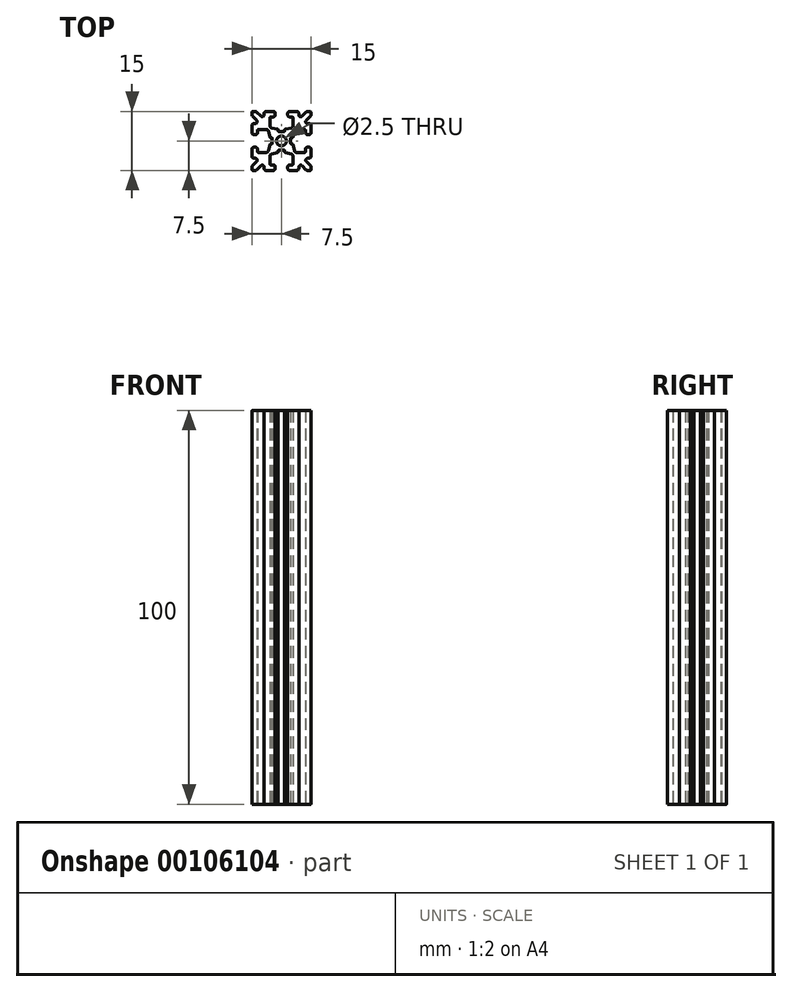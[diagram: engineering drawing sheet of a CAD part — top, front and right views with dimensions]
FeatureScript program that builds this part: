
annotation { "Feature Type Name" : "Feature", "Feature Type Description" : "" }
export const myFeature = defineFeature(function(context is Context, id is Id, definition is map)
    precondition{}
    {
        {
            var Q0;
            Q0=qCreatedBy(makeId("Top.planeOp"),FACE);
            var sketch = newSketch(context, id + "F0", { "sketchPlane" : qUnion([Q0])});
            skCircle(sketch, "E0", {"center": v(0, 0) * mm, "radius": 1.25 * mm});
            skLineSegment(sketch, "E1", {"start": v(0.63, -2.35) * mm, "end": v(-0.63, -2.35) * mm});
            skLineSegment(sketch, "E2", {"start": v(-0.83, -2.55) * mm, "end": v(-0.83, -2.77) * mm});
            skLineSegment(sketch, "E3", {"start": v(-0.98, -2.97) * mm, "end": v(-2.5, -3.31) * mm});
            skLineSegment(sketch, "E4", {"start": v(-2.9, -3.8) * mm, "end": v(-2.9, -5.9) * mm});
            skLineSegment(sketch, "E5", {"start": v(-2.7, -6.1) * mm, "end": v(-2.1, -6.1) * mm});
            skLineSegment(sketch, "E6", {"start": v(-1.6, -6.6) * mm, "end": v(-1.6, -7) * mm});
            skLineSegment(sketch, "E7", {"start": v(-4.4, -7) * mm, "end": v(-4.4, -6.67) * mm});
            skLineSegment(sketch, "E8", {"start": v(-5.25, -6.31) * mm, "end": v(-6.3, -7.35) * mm});
            skLineSegment(sketch, "E9", {"start": v(-7.35, -6.3) * mm, "end": v(-6.31, -5.25) * mm});
            skLineSegment(sketch, "E10", {"start": v(-6.67, -4.4) * mm, "end": v(-7, -4.4) * mm});
            skLineSegment(sketch, "E11", {"start": v(-7.5, -2.1) * mm, "end": v(-7.5, -3.9) * mm});
            skLineSegment(sketch, "E12", {"start": v(-7, -1.6) * mm, "end": v(-6.6, -1.6) * mm});
            skLineSegment(sketch, "E13", {"start": v(-6.1, -2.1) * mm, "end": v(-6.1, -2.7) * mm});
            skLineSegment(sketch, "E14", {"start": v(-5.9, -2.9) * mm, "end": v(-3.8, -2.9) * mm});
            skLineSegment(sketch, "E15", {"start": v(-3.31, -2.5) * mm, "end": v(-2.97, -0.98) * mm});
            skLineSegment(sketch, "E16", {"start": v(-2.77, -0.83) * mm, "end": v(-2.55, -0.83) * mm});
            skLineSegment(sketch, "E17", {"start": v(-2.35, -0.63) * mm, "end": v(-2.35, 0.63) * mm});
            skLineSegment(sketch, "E18", {"start": v(-2.55, 0.83) * mm, "end": v(-2.77, 0.83) * mm});
            skLineSegment(sketch, "E19", {"start": v(-2.97, 0.98) * mm, "end": v(-3.31, 2.5) * mm});
            skLineSegment(sketch, "E20", {"start": v(-3.8, 2.9) * mm, "end": v(-5.9, 2.9) * mm});
            skLineSegment(sketch, "E21", {"start": v(-6.1, 2.7) * mm, "end": v(-6.1, 2.1) * mm});
            skLineSegment(sketch, "E22", {"start": v(-6.6, 1.6) * mm, "end": v(-7, 1.6) * mm});
            skLineSegment(sketch, "E23", {"start": v(-7, 4.4) * mm, "end": v(-6.67, 4.4) * mm});
            skLineSegment(sketch, "E24", {"start": v(-6.31, 5.25) * mm, "end": v(-7.35, 6.3) * mm});
            skLineSegment(sketch, "E25", {"start": v(-6.3, 7.35) * mm, "end": v(-5.25, 6.31) * mm});
            skLineSegment(sketch, "E26", {"start": v(-4.4, 6.67) * mm, "end": v(-4.4, 7) * mm});
            skLineSegment(sketch, "E27", {"start": v(-1.6, 7) * mm, "end": v(-1.6, 6.6) * mm});
            skLineSegment(sketch, "E28", {"start": v(-2.1, 6.1) * mm, "end": v(-2.7, 6.1) * mm});
            skLineSegment(sketch, "E29", {"start": v(-2.9, 5.9) * mm, "end": v(-2.9, 3.8) * mm});
            skLineSegment(sketch, "E30", {"start": v(-2.5, 3.31) * mm, "end": v(-0.98, 2.97) * mm});
            skLineSegment(sketch, "E31", {"start": v(-0.83, 2.77) * mm, "end": v(-0.83, 2.55) * mm});
            skLineSegment(sketch, "E32", {"start": v(-0.63, 2.35) * mm, "end": v(0.63, 2.35) * mm});
            skLineSegment(sketch, "E33", {"start": v(0.83, 2.55) * mm, "end": v(0.83, 2.77) * mm});
            skLineSegment(sketch, "E34", {"start": v(0.98, 2.97) * mm, "end": v(2.5, 3.31) * mm});
            skLineSegment(sketch, "E35", {"start": v(2.9, 3.8) * mm, "end": v(2.9, 5.9) * mm});
            skLineSegment(sketch, "E36", {"start": v(2.7, 6.1) * mm, "end": v(2.1, 6.1) * mm});
            skLineSegment(sketch, "E37", {"start": v(1.6, 6.6) * mm, "end": v(1.6, 7) * mm});
            skLineSegment(sketch, "E38", {"start": v(4.4, 7) * mm, "end": v(4.4, 6.67) * mm});
            skLineSegment(sketch, "E39", {"start": v(5.25, 6.31) * mm, "end": v(6.3, 7.35) * mm});
            skLineSegment(sketch, "E40", {"start": v(7.25, 7.5) * mm, "end": v(6.65, 7.5) * mm});
            skLineSegment(sketch, "E41", {"start": v(7.35, 6.3) * mm, "end": v(6.31, 5.25) * mm});
            skLineSegment(sketch, "E42", {"start": v(6.67, 4.4) * mm, "end": v(7, 4.4) * mm});
            skLineSegment(sketch, "E43", {"start": v(7, 1.6) * mm, "end": v(6.6, 1.6) * mm});
            skLineSegment(sketch, "E44", {"start": v(6.1, 2.1) * mm, "end": v(6.1, 2.7) * mm});
            skLineSegment(sketch, "E45", {"start": v(5.9, 2.9) * mm, "end": v(3.8, 2.9) * mm});
            skLineSegment(sketch, "E46", {"start": v(3.31, 2.5) * mm, "end": v(2.97, 0.98) * mm});
            skLineSegment(sketch, "E47", {"start": v(2.77, 0.83) * mm, "end": v(2.55, 0.83) * mm});
            skLineSegment(sketch, "E48", {"start": v(2.35, 0.63) * mm, "end": v(2.35, -0.63) * mm});
            skLineSegment(sketch, "E49", {"start": v(2.55, -0.83) * mm, "end": v(2.77, -0.83) * mm});
            skLineSegment(sketch, "E50", {"start": v(2.97, -0.98) * mm, "end": v(3.31, -2.5) * mm});
            skLineSegment(sketch, "E51", {"start": v(3.8, -2.9) * mm, "end": v(5.9, -2.9) * mm});
            skLineSegment(sketch, "E52", {"start": v(6.1, -2.7) * mm, "end": v(6.1, -2.1) * mm});
            skLineSegment(sketch, "E53", {"start": v(6.6, -1.6) * mm, "end": v(7, -1.6) * mm});
            skLineSegment(sketch, "E54", {"start": v(7.5, -3.9) * mm, "end": v(7.5, -2.1) * mm});
            skLineSegment(sketch, "E55", {"start": v(7, -4.4) * mm, "end": v(6.67, -4.4) * mm});
            skLineSegment(sketch, "E56", {"start": v(6.31, -5.25) * mm, "end": v(7.35, -6.3) * mm});
            skLineSegment(sketch, "E57", {"start": v(6.65, -7.5) * mm, "end": v(7.25, -7.5) * mm});
            skLineSegment(sketch, "E58", {"start": v(6.3, -7.35) * mm, "end": v(5.25, -6.31) * mm});
            skLineSegment(sketch, "E59", {"start": v(4.4, -6.67) * mm, "end": v(4.4, -7) * mm});
            skLineSegment(sketch, "E60", {"start": v(1.6, -7) * mm, "end": v(1.6, -6.6) * mm});
            skLineSegment(sketch, "E61", {"start": v(2.1, -6.1) * mm, "end": v(2.7, -6.1) * mm});
            skLineSegment(sketch, "E62", {"start": v(2.9, -5.9) * mm, "end": v(2.9, -3.8) * mm});
            skLineSegment(sketch, "E63", {"start": v(2.5, -3.31) * mm, "end": v(0.98, -2.97) * mm});
            skLineSegment(sketch, "E64", {"start": v(0.83, -2.77) * mm, "end": v(0.83, -2.55) * mm});
            skLineSegment(sketch, "E65", {"start": v(-7.5, 3.9) * mm, "end": v(-7.5, 2.1) * mm});
            skLineSegment(sketch, "E66", {"start": v(-6.65, 7.5) * mm, "end": v(-7.25, 7.5) * mm});
            skLineSegment(sketch, "E67", {"start": v(-3.9, -7.5) * mm, "end": v(-2.1, -7.5) * mm});
            skLineSegment(sketch, "E68", {"start": v(7.5, 2.1) * mm, "end": v(7.5, 3.9) * mm});
            skLineSegment(sketch, "E69", {"start": v(-7.5, 7.25) * mm, "end": v(-7.5, 6.65) * mm});
            skLineSegment(sketch, "E70", {"start": v(7.5, -7.25) * mm, "end": v(7.5, -6.65) * mm});
            skLineSegment(sketch, "E71", {"start": v(7.5, 6.65) * mm, "end": v(7.5, 7.25) * mm});
            skLineSegment(sketch, "E72", {"start": v(-2.1, 7.5) * mm, "end": v(-3.9, 7.5) * mm});
            skLineSegment(sketch, "E73", {"start": v(-7.5, -6.65) * mm, "end": v(-7.5, -7.25) * mm});
            skLineSegment(sketch, "E74", {"start": v(3.9, 7.5) * mm, "end": v(2.1, 7.5) * mm});
            skLineSegment(sketch, "E75", {"start": v(2.1, -7.5) * mm, "end": v(3.9, -7.5) * mm});
            skLineSegment(sketch, "E76", {"start": v(-7.25, -7.5) * mm, "end": v(-6.65, -7.5) * mm});
            skArc(sketch, "E77", {"start": v(0.83, -2.55) * mm, "mid": v(0.77, -2.4) * mm, "end": v(0.63, -2.35) * mm});
            skArc(sketch, "E78", {"start": v(-0.63, -2.35) * mm, "mid": v(-0.77, -2.4) * mm, "end": v(-0.83, -2.55) * mm});
            skArc(sketch, "E79", {"start": v(-0.98, -2.97) * mm, "mid": v(-0.87, -2.9) * mm, "end": v(-0.83, -2.77) * mm});
            skArc(sketch, "E80", {"start": v(-2.5, -3.31) * mm, "mid": v(-2.8, -3.49) * mm, "end": v(-2.9, -3.8) * mm});
            skArc(sketch, "E81", {"start": v(-2.9, -5.9) * mm, "mid": v(-2.84, -6.04) * mm, "end": v(-2.7, -6.1) * mm});
            skArc(sketch, "E82", {"start": v(-1.6, -6.6) * mm, "mid": v(-1.75, -6.25) * mm, "end": v(-2.1, -6.1) * mm});
            skArc(sketch, "E83", {"start": v(-2.1, -7.5) * mm, "mid": v(-1.75, -7.35) * mm, "end": v(-1.6, -7) * mm});
            skArc(sketch, "E84", {"start": v(-4.4, -7) * mm, "mid": v(-4.25, -7.35) * mm, "end": v(-3.9, -7.5) * mm});
            skArc(sketch, "E85", {"start": v(-4.4, -6.67) * mm, "mid": v(-4.7, -6.2) * mm, "end": v(-5.25, -6.31) * mm});
            skArc(sketch, "E86", {"start": v(-6.65, -7.5) * mm, "mid": v(-6.46, -7.46) * mm, "end": v(-6.3, -7.35) * mm});
            skArc(sketch, "E87", {"start": v(-7.5, -7.25) * mm, "mid": v(-7.43, -7.43) * mm, "end": v(-7.25, -7.5) * mm});
            skArc(sketch, "E88", {"start": v(-7.35, -6.3) * mm, "mid": v(-7.46, -6.46) * mm, "end": v(-7.5, -6.65) * mm});
            skArc(sketch, "E89", {"start": v(-6.31, -5.25) * mm, "mid": v(-6.2, -4.7) * mm, "end": v(-6.67, -4.4) * mm});
            skArc(sketch, "E90", {"start": v(-7.5, -3.9) * mm, "mid": v(-7.35, -4.25) * mm, "end": v(-7, -4.4) * mm});
            skArc(sketch, "E91", {"start": v(-7, -1.6) * mm, "mid": v(-7.35, -1.75) * mm, "end": v(-7.5, -2.1) * mm});
            skArc(sketch, "E92", {"start": v(-6.1, -2.1) * mm, "mid": v(-6.25, -1.75) * mm, "end": v(-6.6, -1.6) * mm});
            skArc(sketch, "E93", {"start": v(-6.1, -2.7) * mm, "mid": v(-6.04, -2.84) * mm, "end": v(-5.9, -2.9) * mm});
            skArc(sketch, "E94", {"start": v(-3.8, -2.9) * mm, "mid": v(-3.49, -2.8) * mm, "end": v(-3.31, -2.5) * mm});
            skArc(sketch, "E95", {"start": v(-2.77, -0.83) * mm, "mid": v(-2.9, -0.87) * mm, "end": v(-2.97, -0.98) * mm});
            skArc(sketch, "E96", {"start": v(-2.55, -0.83) * mm, "mid": v(-2.4, -0.77) * mm, "end": v(-2.35, -0.63) * mm});
            skArc(sketch, "E97", {"start": v(-2.35, 0.63) * mm, "mid": v(-2.4, 0.77) * mm, "end": v(-2.55, 0.83) * mm});
            skArc(sketch, "E98", {"start": v(-2.97, 0.98) * mm, "mid": v(-2.9, 0.87) * mm, "end": v(-2.77, 0.83) * mm});
            skArc(sketch, "E99", {"start": v(-3.31, 2.5) * mm, "mid": v(-3.49, 2.8) * mm, "end": v(-3.8, 2.9) * mm});
            skArc(sketch, "E100", {"start": v(-5.9, 2.9) * mm, "mid": v(-6.04, 2.84) * mm, "end": v(-6.1, 2.7) * mm});
            skArc(sketch, "E101", {"start": v(-6.6, 1.6) * mm, "mid": v(-6.25, 1.75) * mm, "end": v(-6.1, 2.1) * mm});
            skArc(sketch, "E102", {"start": v(-7.5, 2.1) * mm, "mid": v(-7.35, 1.75) * mm, "end": v(-7, 1.6) * mm});
            skArc(sketch, "E103", {"start": v(-7, 4.4) * mm, "mid": v(-7.35, 4.25) * mm, "end": v(-7.5, 3.9) * mm});
            skArc(sketch, "E104", {"start": v(-6.67, 4.4) * mm, "mid": v(-6.2, 4.7) * mm, "end": v(-6.31, 5.25) * mm});
            skArc(sketch, "E105", {"start": v(-7.5, 6.65) * mm, "mid": v(-7.46, 6.46) * mm, "end": v(-7.35, 6.3) * mm});
            skArc(sketch, "E106", {"start": v(-7.25, 7.5) * mm, "mid": v(-7.43, 7.43) * mm, "end": v(-7.5, 7.25) * mm});
            skArc(sketch, "E107", {"start": v(-6.3, 7.35) * mm, "mid": v(-6.46, 7.46) * mm, "end": v(-6.65, 7.5) * mm});
            skArc(sketch, "E108", {"start": v(-5.25, 6.31) * mm, "mid": v(-4.7, 6.2) * mm, "end": v(-4.4, 6.67) * mm});
            skArc(sketch, "E109", {"start": v(-3.9, 7.5) * mm, "mid": v(-4.25, 7.35) * mm, "end": v(-4.4, 7) * mm});
            skArc(sketch, "E110", {"start": v(-1.6, 7) * mm, "mid": v(-1.75, 7.35) * mm, "end": v(-2.1, 7.5) * mm});
            skArc(sketch, "E111", {"start": v(-2.1, 6.1) * mm, "mid": v(-1.75, 6.25) * mm, "end": v(-1.6, 6.6) * mm});
            skArc(sketch, "E112", {"start": v(-2.7, 6.1) * mm, "mid": v(-2.84, 6.04) * mm, "end": v(-2.9, 5.9) * mm});
            skArc(sketch, "E113", {"start": v(-2.9, 3.8) * mm, "mid": v(-2.8, 3.49) * mm, "end": v(-2.5, 3.31) * mm});
            skArc(sketch, "E114", {"start": v(-0.83, 2.77) * mm, "mid": v(-0.87, 2.9) * mm, "end": v(-0.98, 2.97) * mm});
            skArc(sketch, "E115", {"start": v(-0.83, 2.55) * mm, "mid": v(-0.77, 2.4) * mm, "end": v(-0.63, 2.35) * mm});
            skArc(sketch, "E116", {"start": v(0.63, 2.35) * mm, "mid": v(0.77, 2.4) * mm, "end": v(0.83, 2.55) * mm});
            skArc(sketch, "E117", {"start": v(0.98, 2.97) * mm, "mid": v(0.87, 2.9) * mm, "end": v(0.83, 2.77) * mm});
            skArc(sketch, "E118", {"start": v(2.5, 3.31) * mm, "mid": v(2.8, 3.49) * mm, "end": v(2.9, 3.8) * mm});
            skArc(sketch, "E119", {"start": v(2.9, 5.9) * mm, "mid": v(2.84, 6.04) * mm, "end": v(2.7, 6.1) * mm});
            skArc(sketch, "E120", {"start": v(1.6, 6.6) * mm, "mid": v(1.75, 6.25) * mm, "end": v(2.1, 6.1) * mm});
            skArc(sketch, "E121", {"start": v(2.1, 7.5) * mm, "mid": v(1.75, 7.35) * mm, "end": v(1.6, 7) * mm});
            skArc(sketch, "E122", {"start": v(4.4, 7) * mm, "mid": v(4.25, 7.35) * mm, "end": v(3.9, 7.5) * mm});
            skArc(sketch, "E123", {"start": v(4.4, 6.67) * mm, "mid": v(4.7, 6.2) * mm, "end": v(5.25, 6.31) * mm});
            skArc(sketch, "E124", {"start": v(6.65, 7.5) * mm, "mid": v(6.46, 7.46) * mm, "end": v(6.3, 7.35) * mm});
            skArc(sketch, "E125", {"start": v(7.5, 7.25) * mm, "mid": v(7.43, 7.43) * mm, "end": v(7.25, 7.5) * mm});
            skArc(sketch, "E126", {"start": v(7.35, 6.3) * mm, "mid": v(7.46, 6.46) * mm, "end": v(7.5, 6.65) * mm});
            skArc(sketch, "E127", {"start": v(6.31, 5.25) * mm, "mid": v(6.2, 4.7) * mm, "end": v(6.67, 4.4) * mm});
            skArc(sketch, "E128", {"start": v(7.5, 3.9) * mm, "mid": v(7.35, 4.25) * mm, "end": v(7, 4.4) * mm});
            skArc(sketch, "E129", {"start": v(7, 1.6) * mm, "mid": v(7.35, 1.75) * mm, "end": v(7.5, 2.1) * mm});
            skArc(sketch, "E130", {"start": v(6.1, 2.1) * mm, "mid": v(6.25, 1.75) * mm, "end": v(6.6, 1.6) * mm});
            skArc(sketch, "E131", {"start": v(6.1, 2.7) * mm, "mid": v(6.04, 2.84) * mm, "end": v(5.9, 2.9) * mm});
            skArc(sketch, "E132", {"start": v(3.8, 2.9) * mm, "mid": v(3.49, 2.8) * mm, "end": v(3.31, 2.5) * mm});
            skArc(sketch, "E133", {"start": v(2.77, 0.83) * mm, "mid": v(2.9, 0.87) * mm, "end": v(2.97, 0.98) * mm});
            skArc(sketch, "E134", {"start": v(2.55, 0.83) * mm, "mid": v(2.4, 0.77) * mm, "end": v(2.35, 0.63) * mm});
            skArc(sketch, "E135", {"start": v(2.35, -0.63) * mm, "mid": v(2.4, -0.77) * mm, "end": v(2.55, -0.83) * mm});
            skArc(sketch, "E136", {"start": v(2.97, -0.98) * mm, "mid": v(2.9, -0.87) * mm, "end": v(2.77, -0.83) * mm});
            skArc(sketch, "E137", {"start": v(3.31, -2.5) * mm, "mid": v(3.49, -2.8) * mm, "end": v(3.8, -2.9) * mm});
            skArc(sketch, "E138", {"start": v(5.9, -2.9) * mm, "mid": v(6.04, -2.84) * mm, "end": v(6.1, -2.7) * mm});
            skArc(sketch, "E139", {"start": v(6.6, -1.6) * mm, "mid": v(6.25, -1.75) * mm, "end": v(6.1, -2.1) * mm});
            skArc(sketch, "E140", {"start": v(7.5, -2.1) * mm, "mid": v(7.35, -1.75) * mm, "end": v(7, -1.6) * mm});
            skArc(sketch, "E141", {"start": v(7, -4.4) * mm, "mid": v(7.35, -4.25) * mm, "end": v(7.5, -3.9) * mm});
            skArc(sketch, "E142", {"start": v(6.67, -4.4) * mm, "mid": v(6.2, -4.7) * mm, "end": v(6.31, -5.25) * mm});
            skArc(sketch, "E143", {"start": v(7.5, -6.65) * mm, "mid": v(7.46, -6.46) * mm, "end": v(7.35, -6.3) * mm});
            skArc(sketch, "E144", {"start": v(7.25, -7.5) * mm, "mid": v(7.43, -7.43) * mm, "end": v(7.5, -7.25) * mm});
            skArc(sketch, "E145", {"start": v(6.3, -7.35) * mm, "mid": v(6.46, -7.46) * mm, "end": v(6.65, -7.5) * mm});
            skArc(sketch, "E146", {"start": v(5.25, -6.31) * mm, "mid": v(4.7, -6.2) * mm, "end": v(4.4, -6.67) * mm});
            skArc(sketch, "E147", {"start": v(3.9, -7.5) * mm, "mid": v(4.25, -7.35) * mm, "end": v(4.4, -7) * mm});
            skArc(sketch, "E148", {"start": v(1.6, -7) * mm, "mid": v(1.75, -7.35) * mm, "end": v(2.1, -7.5) * mm});
            skArc(sketch, "E149", {"start": v(2.1, -6.1) * mm, "mid": v(1.75, -6.25) * mm, "end": v(1.6, -6.6) * mm});
            skArc(sketch, "E150", {"start": v(2.7, -6.1) * mm, "mid": v(2.84, -6.04) * mm, "end": v(2.9, -5.9) * mm});
            skArc(sketch, "E151", {"start": v(2.9, -3.8) * mm, "mid": v(2.8, -3.49) * mm, "end": v(2.5, -3.31) * mm});
            skArc(sketch, "E152", {"start": v(0.83, -2.77) * mm, "mid": v(0.87, -2.9) * mm, "end": v(0.98, -2.97) * mm});
            skSolve(sketch);
        }
        {
            var Q0;
            Q0 = qSketchRegion(id + "F0", true);
            extrude(context, id + "F1", {"entities" : qUnion([Q0]), "depth" : 100 * mm});
        }
    });
